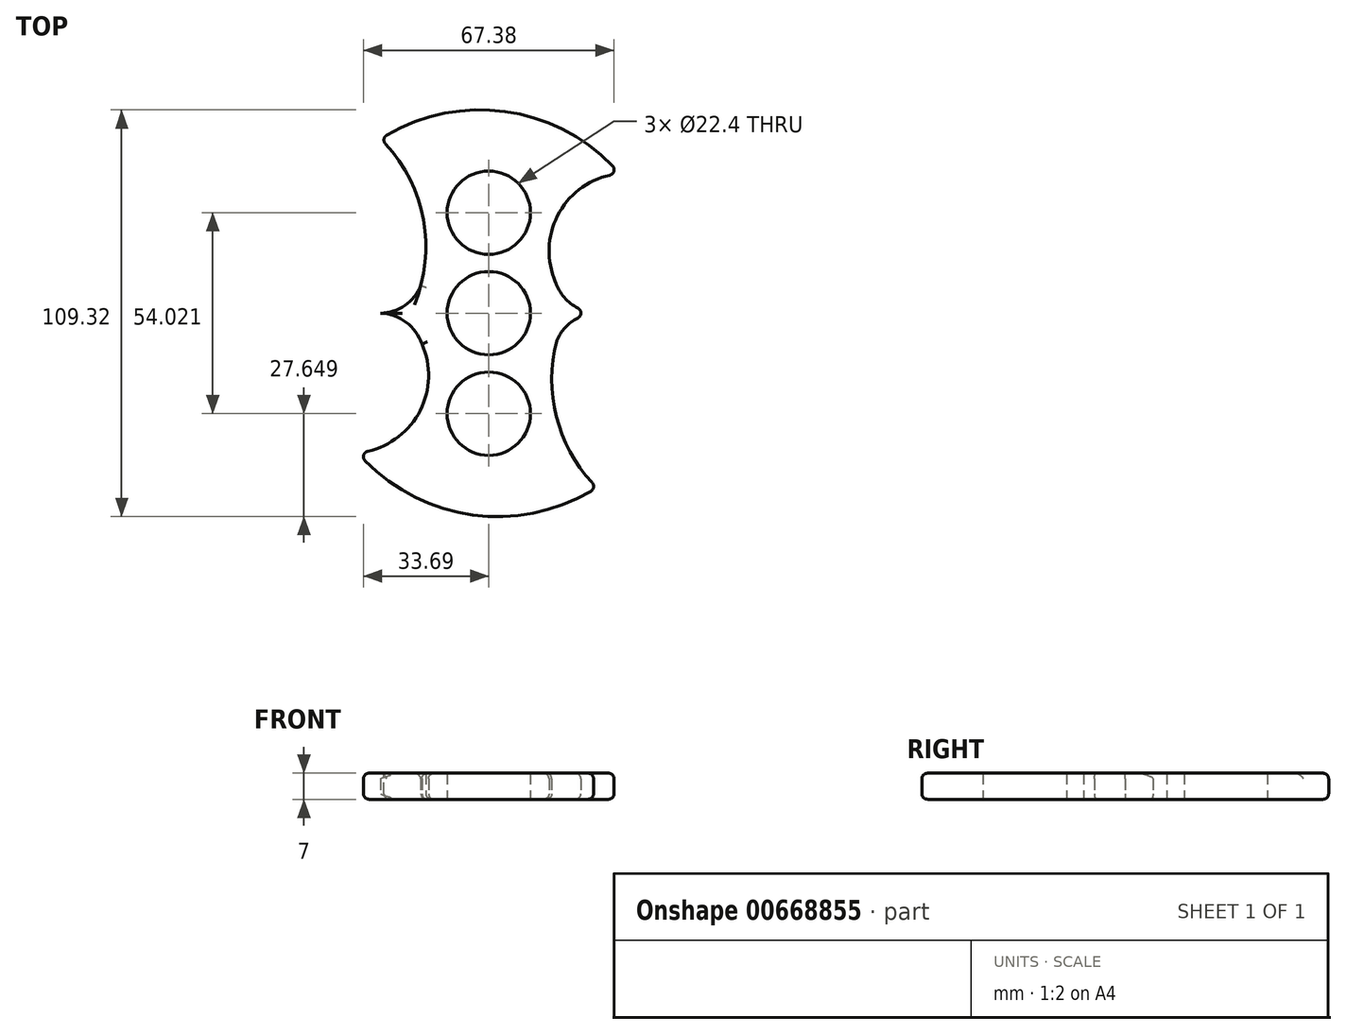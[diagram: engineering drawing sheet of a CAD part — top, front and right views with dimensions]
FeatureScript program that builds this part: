
annotation { "Feature Type Name" : "Feature", "Feature Type Description" : "" }
export const myFeature = defineFeature(function(context is Context, id is Id, definition is map)
    precondition{}
    {
        {
            var Q0;
            Q0=qCreatedBy(makeId("Top.planeOp"),FACE);
            var sketch = newSketch(context, id + "F0", { "sketchPlane" : qUnion([Q0])});
            skCircle(sketch, "E0", {"center": v(0, 0) * mm, "radius": 11.2 * mm});
            skCircle(sketch, "E1", {"center": v(0, 0) * mm, "radius": 13.2 * mm});
            skCircle(sketch, "E2", {"center": v(0, 27.01) * mm, "radius": 11.2 * mm});
            skCircle(sketch, "E3", {"center": v(0, 27.01) * mm, "radius": 13.2 * mm});
            skCircle(sketch, "E4.1.0", {"center": v(0, -27.01) * mm, "radius": 11.2 * mm});
            skCircle(sketch, "E4.1.1", {"center": v(0, -27.01) * mm, "radius": 13.2 * mm});
            skArc(sketch, "E5", {"start": v(35.19, 37.52) * mm, "mid": v(4.8, 54.14) * mm, "end": v(-29.05, 46.87) * mm});
            skArc(sketch, "E6", {"start": v(35.19, 37.52) * mm, "mid": v(19.09, 27.34) * mm, "end": v(17.96, 8.32) * mm});
            skArc(sketch, "E7.1.0", {"start": v(-35.19, -37.52) * mm, "mid": v(-4.8, -54.14) * mm, "end": v(29.05, -46.87) * mm});
            skArc(sketch, "E8.1.0", {"start": v(-35.19, -37.52) * mm, "mid": v(-19.09, -27.34) * mm, "end": v(-17.96, -8.32) * mm});
            skArc(sketch, "E9", {"start": v(18.25, -7.45) * mm, "mid": v(18.37, -28.6) * mm, "end": v(29.05, -46.87) * mm});
            skArc(sketch, "E10.1.0", {"start": v(-18.25, 7.45) * mm, "mid": v(-18.37, 28.6) * mm, "end": v(-29.05, 46.87) * mm});
            skArc(sketch, "E11", {"start": v(17.96, 8.32) * mm, "mid": v(22.58, 2.2) * mm, "end": v(29.93, 0) * mm});
            skArc(sketch, "E12", {"start": v(29.93, 0) * mm, "mid": v(22.91, -1.88) * mm, "end": v(18.25, -7.45) * mm});
            skArc(sketch, "E13.1.0", {"start": v(-17.96, -8.32) * mm, "mid": v(-22.58, -2.2) * mm, "end": v(-29.93, 0) * mm});
            skArc(sketch, "E13.1.1", {"start": v(-29.93, 0) * mm, "mid": v(-22.91, 1.88) * mm, "end": v(-18.25, 7.45) * mm});
            skSolve(sketch);
        }
        {
            var Q0;
            Q0=makeQuery(id+"F0.imprint","IMPRINT",FACE,{"disambiguationData":[TD([[makeQuery(id+"F0.imprint","IMPRINT",EDGE,{"derivedFrom":sQuery(id+"F0.wireOp",EDGE,"E1")}),-1.0]])]});
            var Q1;
            Q1=makeQuery(id+"F0.imprint","IMPRINT",FACE,{"disambiguationData":[TD([[makeQuery(id+"F0.imprint","IMPRINT",EDGE,{"derivedFrom":sQuery(id+"F0.wireOp",EDGE,"E2")}),-1.0]])]});
            var Q2;
            Q2=makeQuery(id+"F0.imprint","IMPRINT",FACE,{"disambiguationData":[TD([[makeQuery(id+"F0.imprint","IMPRINT",EDGE,{"derivedFrom":sQuery(id+"F0.wireOp",EDGE,"E0")}),-1.0]])]});
            var Q3;
            Q3=makeQuery(id+"F0.imprint","IMPRINT",FACE,{"disambiguationData":[TD([[makeQuery(id+"F0.imprint","IMPRINT",EDGE,{"derivedFrom":sQuery(id+"F0.wireOp",EDGE,"E4.1.0")}),-1.0]])]});
            extrude(context, id + "F1", {"entities" : qUnion([Q0, Q1, Q2, Q3]), "depth" : 7 * mm, "offsetDistance" : 25 * mm});
        }
        {
            var Q0;
            Q0=makeQuery(id+"F1.opExtrude","SWEPT_FACE",FACE,{"disambiguationData":[OSD([sQuery(id+"F0.wireOp",EDGE,"E7.1.0")])]});
            var Q1;
            Q1=makeQuery(id+"F1.opExtrude","SWEPT_FACE",FACE,{"disambiguationData":[OSD([sQuery(id+"F0.wireOp",EDGE,"E6")])]});
            var Q2;
            Q2=makeQuery(id+"F1.opExtrude","SWEPT_FACE",FACE,{"disambiguationData":[OSD([sQuery(id+"F0.wireOp",EDGE,"E9")])]});
            var Q3;
            Q3=makeQuery(id+"F1.opExtrude","SWEPT_FACE",FACE,{"disambiguationData":[OSD([sQuery(id+"F0.wireOp",EDGE,"E11")])]});
            var Q4;
            Q4=makeQuery(id+"F1.opExtrude","SWEPT_FACE",FACE,{"disambiguationData":[OSD([sQuery(id+"F0.wireOp",EDGE,"E12")])]});
            var Q5;
            Q5=makeQuery(id+"F1.opExtrude","SWEPT_FACE",FACE,{"disambiguationData":[OSD([sQuery(id+"F0.wireOp",EDGE,"E5")])]});
            var Q6;
            Q6=makeQuery(id+"F1.opExtrude","CAP_EDGE",EDGE,{"disambiguationData":[OSD([sQuery(id+"F0.wireOp",EDGE,"E13.1.0")])],"isStart":true});
            var Q7;
            Q7=makeQuery(id+"F1.opExtrude","CAP_EDGE",EDGE,{"disambiguationData":[OSD([sQuery(id+"F0.wireOp",EDGE,"E8.1.0")])],"isStart":true});
            var Q8;
            Q8=makeQuery(id+"F1.opExtrude","CAP_EDGE",EDGE,{"disambiguationData":[OSD([sQuery(id+"F0.wireOp",EDGE,"E10.1.0")])],"isStart":true});
            var Q9;
            Q9=makeQuery(id+"F1.opExtrude","CAP_EDGE",EDGE,{"disambiguationData":[OSD([sQuery(id+"F0.wireOp",EDGE,"E13.1.1")])],"isStart":true});
            var Q10;
            Q10=makeQuery(id+"F1.opExtrude","CAP_EDGE",EDGE,{"disambiguationData":[OSD([sQuery(id+"F0.wireOp",EDGE,"E13.1.1")])],"isStart":false});
            var Q11;
            Q11=makeQuery(id+"F1.opExtrude","CAP_EDGE",EDGE,{"disambiguationData":[OSD([sQuery(id+"F0.wireOp",EDGE,"E8.1.0")])],"isStart":false});
            fillet(context, id + "F2", {"entities" : qUnion([Q0, Q1, Q2, Q3, Q4, Q5, Q6, Q7, Q8, Q9, Q10, Q11]), "radius" : 1.5 * mm, "tangentPropagation" : true, "allowEdgeOverflow" : false});
        }
    });
